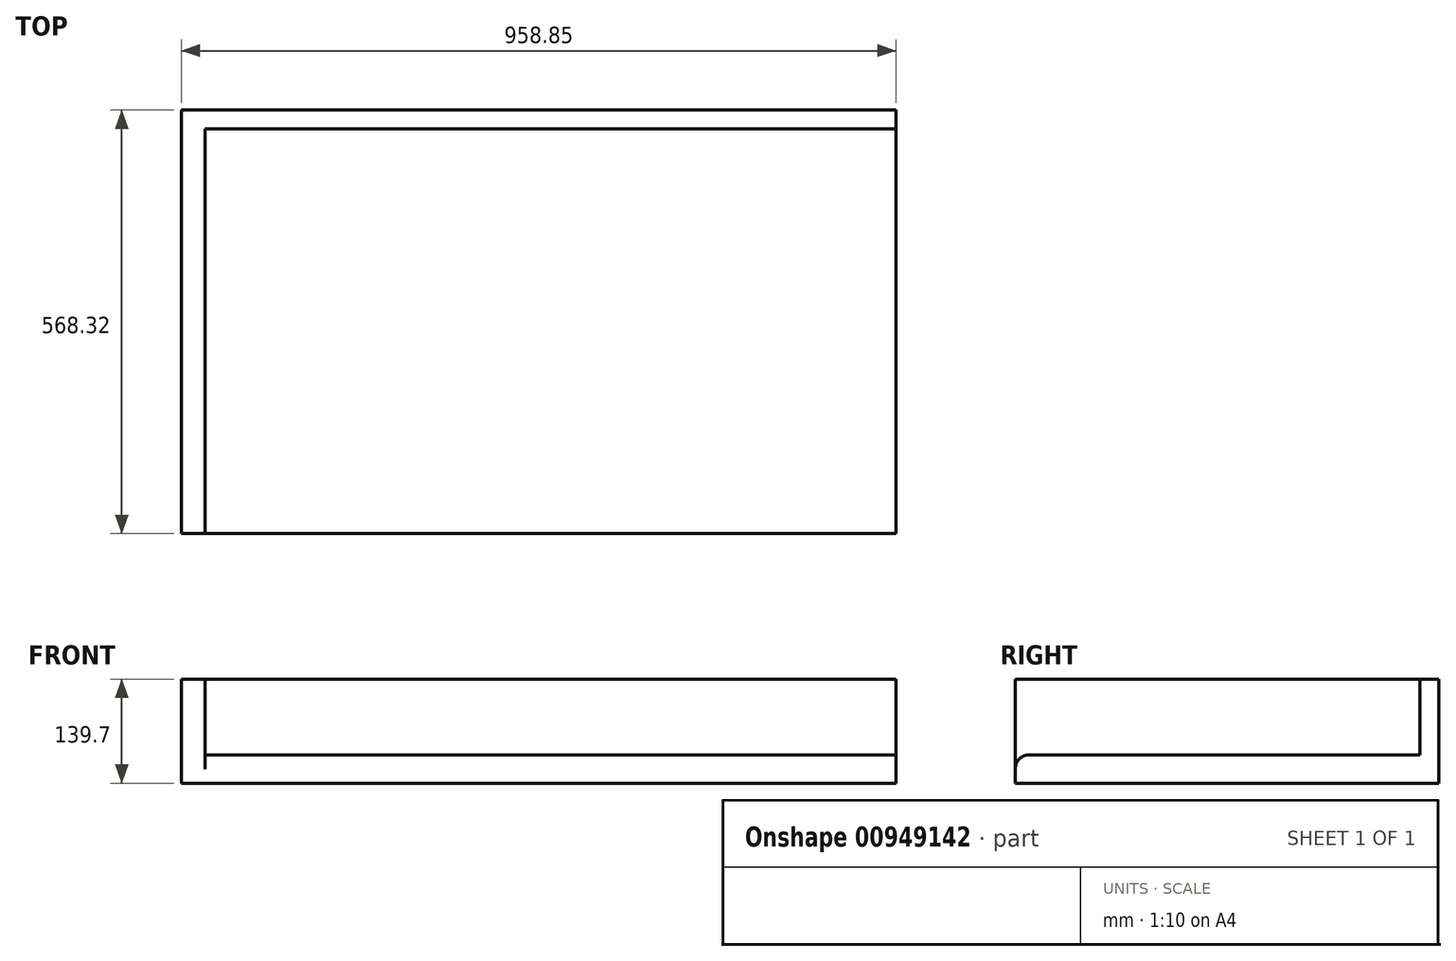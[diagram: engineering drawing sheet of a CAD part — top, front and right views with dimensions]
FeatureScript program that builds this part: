
annotation { "Feature Type Name" : "Feature", "Feature Type Description" : "" }
export const myFeature = defineFeature(function(context is Context, id is Id, definition is map)
    precondition{}
    {
        {
            var Q0;
            Q0=qCreatedBy(makeId("Front.planeOp"),FACE);
            var sketch = newSketch(context, id + "F0", { "sketchPlane" : qUnion([Q0])});
            skLineSegment(sketch, "E0.bottom", {"start": v(463.55, -19.05) * mm, "end": v(-463.55, -19.05) * mm});
            skLineSegment(sketch, "E0.top", {"start": v(463.55, 19.05) * mm, "end": v(-463.55, 19.05) * mm});
            skLineSegment(sketch, "E0.left", {"start": v(463.55, -19.05) * mm, "end": v(463.55, 19.05) * mm});
            skLineSegment(sketch, "E0.right", {"start": v(-463.55, -19.05) * mm, "end": v(-463.55, 19.05) * mm});
            skPoint(sketch, "E0.middle", {"position": v(0, 0) * mm});
            skSolve(sketch);
        }
        {
            var Q0;
            Q0=makeQuery(id+"F0.imprint","IMPRINT",FACE,{"disambiguationData":[TD([[makeQuery(id+"F0.imprint","IMPRINT",EDGE,{"derivedFrom":sQuery(id+"F0.wireOp",EDGE,"E0.bottom")}),-1.0]])]});
            extrude(context, id + "F1", {"entities" : qUnion([Q0]), "depth" : 542.92 * mm, "offsetDistance" : 25.4 * mm});
        }
        {
            var Q0;
            Q0=makeQuery(id+"F1.opExtrude","SWEPT_FACE",FACE,{"disambiguationData":[OSD([sQuery(id+"F0.wireOp",EDGE,"E0.top")])]});
            var sketch = newSketch(context, id + "F2", { "sketchPlane" : qUnion([Q0])});
            skEllipse(sketch, "E1", {"center": v(0, -228.6) * mm, "majorRadius": 228.6 * mm, "minorRadius": 177.8 * mm, "majorAxis": v(1, 0)});
            skSolve(sketch);
        }
        {
            var Q0;
            Q0=qCreatedBy(makeId("Top.planeOp"),FACE);
            var sketch = newSketch(context, id + "F3", { "sketchPlane" : qUnion([Q0])});
            skLineSegment(sketch, "E2.bottom", {"start": v(-495.3, 25.4) * mm, "end": v(-463.55, 25.4) * mm});
            skLineSegment(sketch, "E2.top", {"start": v(-495.3, -542.92) * mm, "end": v(-463.55, -542.92) * mm});
            skLineSegment(sketch, "E2.left", {"start": v(-495.3, 25.4) * mm, "end": v(-495.3, -542.93) * mm});
            skLineSegment(sketch, "E2.right", {"start": v(-463.55, 25.4) * mm, "end": v(-463.55, -542.92) * mm});
            skSolve(sketch);
        }
        {
            var Q0;
            Q0=makeQuery(id+"F3.imprint","IMPRINT",FACE,{"disambiguationData":[TD([[makeQuery(id+"F3.imprint","IMPRINT",EDGE,{"derivedFrom":sQuery(id+"F3.wireOp",EDGE,"E2.bottom")}),-1.0]])]});
            var Q1;
            Q1=makeQuery(id+"F1.opExtrude","SWEPT_FACE",FACE,{"disambiguationData":[OSD([sQuery(id+"F0.wireOp",EDGE,"E0.bottom")])]});
            extrude(context, id + "F4", {"entities" : qUnion([Q0]), "operationType" : NewBodyOperationType.ADD, "depth" : 120.65 * mm, "offsetDistance" : 25.4 * mm, "hasSecondDirection" : true, "secondDirectionBound" : SecondDirectionBoundingType.UP_TO_SURFACE, "secondDirectionOppositeDirection" : true, "secondDirectionDepth" : 25.4 * mm, "secondDirectionBoundEntityFace" : qUnion([Q1])});
        }
        {
            var Q0;
            Q0=qCreatedBy(makeId("Top.planeOp"),FACE);
            var sketch = newSketch(context, id + "F5", { "sketchPlane" : qUnion([Q0])});
            skLineSegment(sketch, "E3.bottom", {"start": v(463.55, 0) * mm, "end": v(-463.55, 0) * mm});
            skLineSegment(sketch, "E3.top", {"start": v(463.55, 25.4) * mm, "end": v(-463.55, 25.4) * mm});
            skLineSegment(sketch, "E3.left", {"start": v(463.55, 0) * mm, "end": v(463.55, 25.4) * mm});
            skLineSegment(sketch, "E3.right", {"start": v(-463.55, 0) * mm, "end": v(-463.55, 25.4) * mm});
            skSolve(sketch);
        }
        {
            var Q0;
            Q0=makeQuery(id+"F5.imprint","IMPRINT",FACE,{"disambiguationData":[TD([[makeQuery(id+"F5.imprint","IMPRINT",EDGE,{"derivedFrom":sQuery(id+"F5.wireOp",EDGE,"E3.bottom")}),-1.0]])]});
            var Q1;
            Q1=makeQuery(id+"F4.boolean.opBoolean","MERGE",FACE,{"derivedFrom":[makeQuery(id+"F1.opExtrude","SWEPT_FACE",FACE,{"disambiguationData":[OSD([sQuery(id+"F0.wireOp",EDGE,"E0.bottom")])]}),makeQuery(id+"F4.opExtrude","CAP_FACE",FACE,{"disambiguationData":[OSD([sQuery(id+"F3.wireOp",EDGE,"E2.bottom"),sQuery(id+"F3.wireOp",EDGE,"E2.top"),sQuery(id+"F3.wireOp",EDGE,"E2.left"),sQuery(id+"F3.wireOp",EDGE,"E2.right")])],"isStart":true})]});
            extrude(context, id + "F6", {"entities" : qUnion([Q0]), "operationType" : NewBodyOperationType.ADD, "depth" : 120.65 * mm, "offsetDistance" : 25.4 * mm, "hasSecondDirection" : true, "secondDirectionBound" : SecondDirectionBoundingType.UP_TO_SURFACE, "secondDirectionOppositeDirection" : true, "secondDirectionDepth" : 25.4 * mm, "secondDirectionBoundEntityFace" : qUnion([Q1])});
        }
        {
            var Q0;
            Q0=makeQuery(id+"F1.opExtrude","CAP_EDGE",EDGE,{"disambiguationData":[OSD([sQuery(id+"F0.wireOp",EDGE,"E0.top")])],"isStart":false});
            fillet(context, id + "F7", {"entities" : qUnion([Q0]), "radius" : 19.05 * mm, "tangentPropagation" : true, "allowEdgeOverflow" : false});
        }
    });
